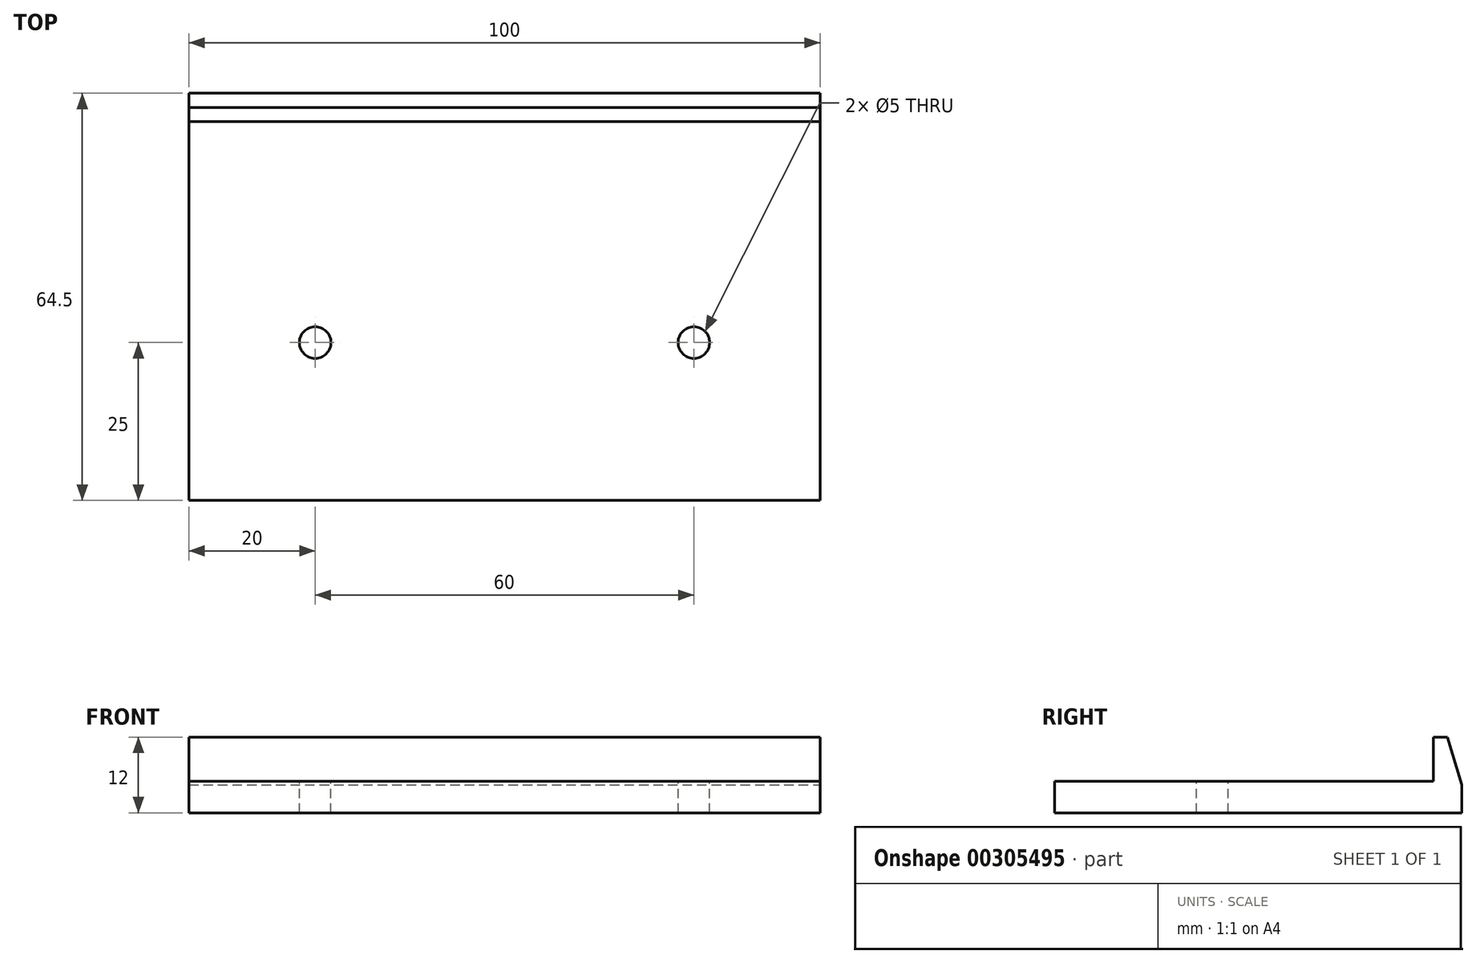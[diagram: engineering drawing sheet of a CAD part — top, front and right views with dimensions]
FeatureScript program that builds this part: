
annotation { "Feature Type Name" : "Feature", "Feature Type Description" : "" }
export const myFeature = defineFeature(function(context is Context, id is Id, definition is map)
    precondition{}
    {
        {
            var Q0;
            Q0=qCreatedBy(makeId("Right.planeOp"),FACE);
            var sketch = newSketch(context, id + "F0", { "sketchPlane" : qUnion([Q0])});
            skLineSegment(sketch, "E0", {"start": v(0, 0) * mm, "end": v(0, 12) * mm});
            skLineSegment(sketch, "E1", {"start": v(0, 12) * mm, "end": v(-4.5, 12) * mm});
            skLineSegment(sketch, "E2", {"start": v(-4.5, 12) * mm, "end": v(-4.5, 5) * mm});
            skLineSegment(sketch, "E3", {"start": v(-4.5, 5) * mm, "end": v(-64.5, 5) * mm});
            skLineSegment(sketch, "E4", {"start": v(-64.5, 5) * mm, "end": v(-64.5, 0) * mm});
            skLineSegment(sketch, "E5", {"start": v(-64.5, 0) * mm, "end": v(0, 0) * mm});
            skSolve(sketch);
        }
        {
            var Q0;
            Q0=makeQuery(id+"F0.imprint","IMPRINT",FACE,{"disambiguationData":[TD([[makeQuery(id+"F0.imprint","IMPRINT",EDGE,{"derivedFrom":sQuery(id+"F0.wireOp",EDGE,"E0")}),1.0]])]});
            extrude(context, id + "F1", {"entities" : qUnion([Q0]), "endBound" : BoundingType.SYMMETRIC, "depth" : 100 * mm});
        }
        {
            var Q0;
            Q0=makeQuery(id+"F1.opExtrude","CAP_FACE",FACE,{"disambiguationData":[OSD([sQuery(id+"F0.wireOp",EDGE,"E0"),sQuery(id+"F0.wireOp",EDGE,"E1"),sQuery(id+"F0.wireOp",EDGE,"E2"),sQuery(id+"F0.wireOp",EDGE,"E3"),sQuery(id+"F0.wireOp",EDGE,"E4"),sQuery(id+"F0.wireOp",EDGE,"E5")])],"isStart":false});
            var sketch = newSketch(context, id + "F2", { "sketchPlane" : qUnion([Q0])});
            skLineSegment(sketch, "E6", {"start": v(-2.25, 12) * mm, "end": v(0, 4.41) * mm});
            skLineSegment(sketch, "E7", {"start": v(0, 4.41) * mm, "end": v(0, 12) * mm});
            skLineSegment(sketch, "E8", {"start": v(0, 12) * mm, "end": v(-2.25, 12) * mm});
            skSolve(sketch);
        }
        {
            var Q0;
            Q0=makeQuery(id+"F2.imprint","IMPRINT",FACE,{"disambiguationData":[TD([[makeQuery(id+"F2.imprint","IMPRINT",EDGE,{"derivedFrom":sQuery(id+"F2.wireOp",EDGE,"E6")}),1.0]])]});
            extrude(context, id + "F3", {"entities" : qUnion([Q0]), "operationType" : NewBodyOperationType.REMOVE, "endBound" : BoundingType.UP_TO_NEXT, "oppositeDirection" : true, "depth" : 100 * mm});
        }
        {
            var Q0;
            Q0=makeQuery(id+"F1.opExtrude","SWEPT_FACE",FACE,{"disambiguationData":[OSD([sQuery(id+"F0.wireOp",EDGE,"E3")])]});
            var sketch = newSketch(context, id + "F4", { "sketchPlane" : qUnion([Q0])});
            skLineSegment(sketch, "E9", {"start": v(-50, -64.5) * mm, "end": v(-50, -39.5) * mm, "construction": true});
            skLineSegment(sketch, "E10", {"start": v(-50, -39.5) * mm, "end": v(-30, -39.5) * mm, "construction": true});
            skLineSegment(sketch, "E11", {"start": v(-30, -39.5) * mm, "end": v(30, -39.5) * mm, "construction": true});
            skCircle(sketch, "E12", {"center": v(-30, -39.5) * mm, "radius": 2.5 * mm});
            skCircle(sketch, "E13", {"center": v(30, -39.5) * mm, "radius": 2.5 * mm});
            skSolve(sketch);
        }
        {
            var Q0;
            Q0=makeQuery(id+"F4.imprint","IMPRINT",FACE,{"disambiguationData":[TD([[makeQuery(id+"F4.imprint","IMPRINT",EDGE,{"derivedFrom":sQuery(id+"F4.wireOp",EDGE,"E12")}),1.0]])]});
            var Q1;
            Q1=makeQuery(id+"F4.imprint","IMPRINT",FACE,{"disambiguationData":[TD([[makeQuery(id+"F4.imprint","IMPRINT",EDGE,{"derivedFrom":sQuery(id+"F4.wireOp",EDGE,"E13")}),1.0]])]});
            extrude(context, id + "F5", {"entities" : qUnion([Q0, Q1]), "operationType" : NewBodyOperationType.REMOVE, "endBound" : BoundingType.UP_TO_NEXT, "oppositeDirection" : true, "depth" : 25 * mm});
        }
    });
